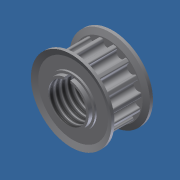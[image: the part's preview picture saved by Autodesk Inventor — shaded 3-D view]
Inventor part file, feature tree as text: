
AUTODESK INVENTOR PART (.ipt)
format: ipt  version: 2012 (Build 160160000, 160)  size: 313,856 bytes
history: native  units: in
note: dims shown in document units (in); Inventor stores cm internally (conversion verified against a paired STEP export)
features: extrude x3, sketch x2, thread x1, imported_body x1, projected_geometry x1
ambient origin geometry x8: Origin, YZ Plane, XZ Plane, XY Plane, X Axis, Y Axis, Z Axis, Center Point
feature tree (8):
  sketch  "Sketch1"  dims[d0=0.5in d1=3.937in d2=0.0in]
  extrude  "Extrusion1"  Depth=3.937in TaperAngle=0.0deg
  extrude  "Extrusion2"  Depth=0.2106in
  extrude  "Extrusion3"  Depth=0.0787in
  thread  "Thread1"  [1 undecoded]
  imported_body  "Base1"
  projected_geometry  "Projected Loop1"
  sketch  "Sketch3"  dims[d3=0.1969in d4=0.0in d10=0.2106in d11=0.0787in d12=0.0787in d14=0.0394in d15=0.1969in d16=0.0in d17=0.3937in d18=0.0in]
note: 1 required parameter value undecoded (feature->parameter linkage not recoverable at this tier; creation-order binding heuristic only, values carry confidence <= 0.55)
